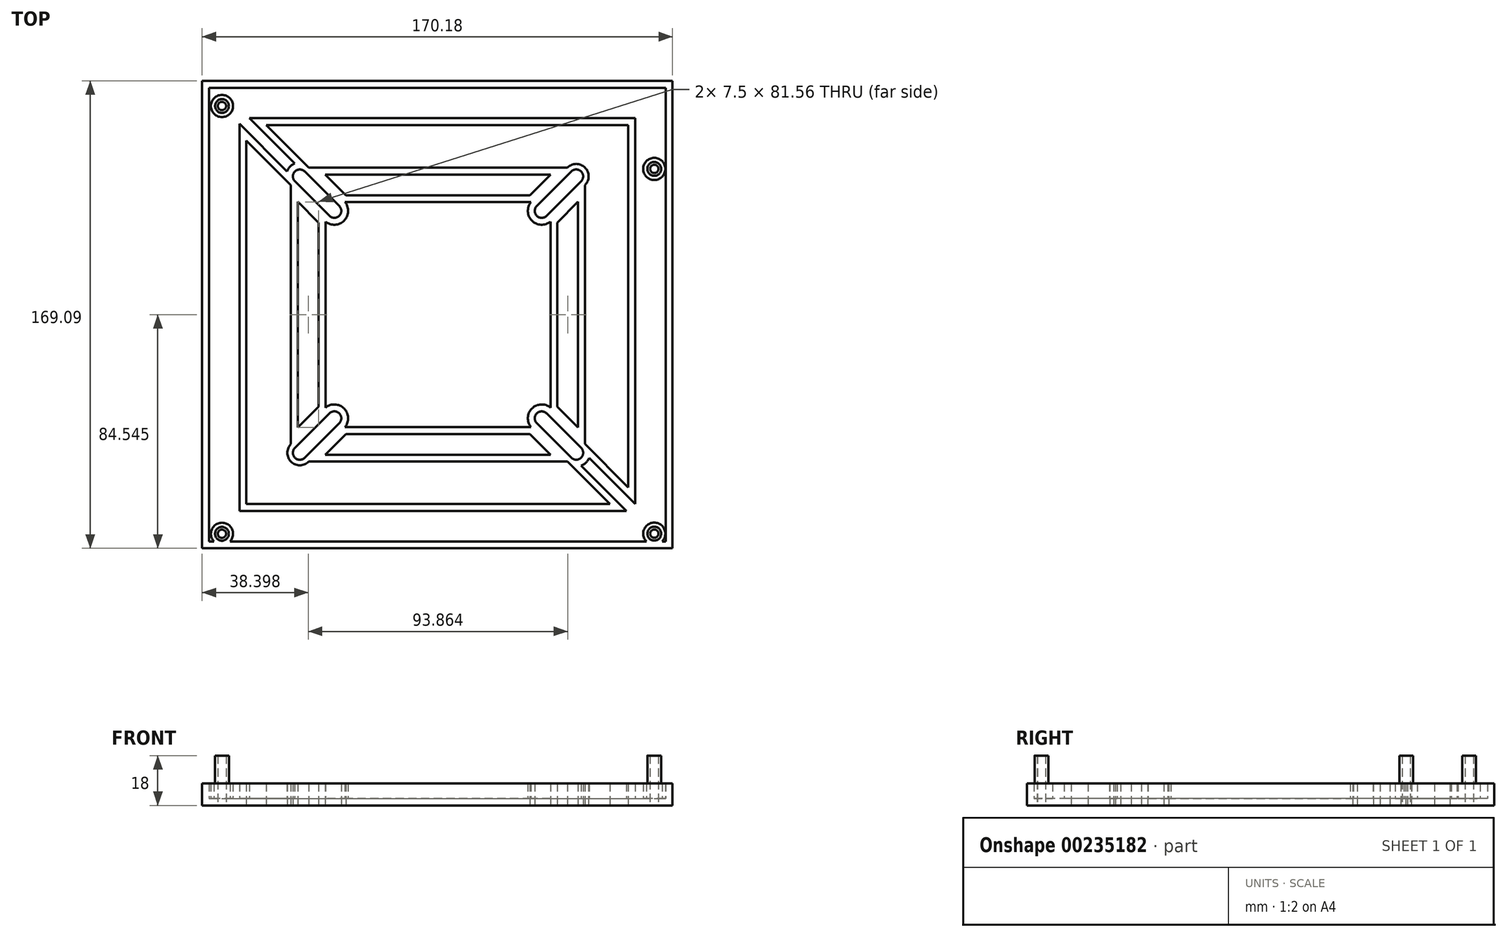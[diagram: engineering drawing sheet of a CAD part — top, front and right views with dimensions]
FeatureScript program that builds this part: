
annotation { "Feature Type Name" : "Feature", "Feature Type Description" : "" }
export const myFeature = defineFeature(function(context is Context, id is Id, definition is map)
    precondition{}
    {
        {
            var Q0;
            Q0=qCreatedBy(makeId("Top.planeOp"),FACE);
            var sketch = newSketch(context, id + "F0", { "sketchPlane" : qUnion([Q0])});
            skLineSegment(sketch, "E0.bottom", {"start": v(-27.19, 83.65) * mm, "end": v(142.99, 83.65) * mm});
            skLineSegment(sketch, "E0.top", {"start": v(-27.19, -85.44) * mm, "end": v(142.99, -85.44) * mm});
            skLineSegment(sketch, "E0.left", {"start": v(-27.19, 83.65) * mm, "end": v(-27.19, -85.44) * mm});
            skLineSegment(sketch, "E0.right", {"start": v(142.99, 83.65) * mm, "end": v(142.99, -85.44) * mm});
            skCircle(sketch, "E1", {"center": v(136.38, -80.15) * mm, "radius": 2.5 * mm});
            skCircle(sketch, "E2.0", {"center": v(136.38, -80.15) * mm, "radius": 1.5 * mm});
            skCircle(sketch, "E3", {"center": v(-20.03, -80.18) * mm, "radius": 2.5 * mm});
            skCircle(sketch, "E4.0", {"center": v(-20.03, -80.18) * mm, "radius": 1.5 * mm});
            skCircle(sketch, "E5", {"center": v(-20.02, 74.56) * mm, "radius": 2.5 * mm});
            skCircle(sketch, "E6.0", {"center": v(-20.02, 74.56) * mm, "radius": 1.5 * mm});
            skCircle(sketch, "E7", {"center": v(136.38, 51.8) * mm, "radius": 2.5 * mm});
            skCircle(sketch, "E8.0", {"center": v(136.38, 51.8) * mm, "radius": 1.5 * mm});
            skLineSegment(sketch, "E9.bottom", {"start": v(8.14, 49.1) * mm, "end": v(58.14, 49.1) * mm, "construction": true});
            skLineSegment(sketch, "E9.top", {"start": v(8.14, -50.9) * mm, "end": v(108.14, -50.9) * mm, "construction": true});
            skLineSegment(sketch, "E9.left", {"start": v(8.14, 49.1) * mm, "end": v(8.14, -0.9) * mm, "construction": true});
            skLineSegment(sketch, "E9.right", {"start": v(108.14, 49.1) * mm, "end": v(108.14, -0.9) * mm, "construction": true});
            skLineSegment(sketch, "E10.0", {"start": v(20.64, 36.6) * mm, "end": v(58.14, 36.6) * mm, "construction": true});
            skLineSegment(sketch, "E10.1", {"start": v(20.64, 36.6) * mm, "end": v(20.64, -0.9) * mm, "construction": true});
            skLineSegment(sketch, "E10.2", {"start": v(20.64, -38.4) * mm, "end": v(95.64, -38.4) * mm, "construction": true});
            skLineSegment(sketch, "E10.3", {"start": v(95.64, 36.6) * mm, "end": v(95.64, -0.9) * mm, "construction": true});
            skLineSegment(sketch, "E11", {"start": v(9.9, 50.87) * mm, "end": v(9.9, 50.87) * mm});
            skLineSegment(sketch, "E12", {"start": v(18.87, 34.84) * mm, "end": v(6.37, 47.34) * mm});
            skLineSegment(sketch, "E13", {"start": v(9.9, 50.87) * mm, "end": v(22.4, 38.37) * mm});
            skArc(sketch, "E14", {"start": v(6.37, 47.34) * mm, "mid": v(9.9, 47.34) * mm, "end": v(9.9, 50.87) * mm});
            skArc(sketch, "E15", {"start": v(9.9, 50.87) * mm, "mid": v(6.37, 50.87) * mm, "end": v(6.37, 47.34) * mm});
            skArc(sketch, "E16", {"start": v(22.4, 38.37) * mm, "mid": v(18.87, 38.37) * mm, "end": v(18.87, 34.84) * mm});
            skArc(sketch, "E17", {"start": v(18.87, 34.84) * mm, "mid": v(22.4, 34.84) * mm, "end": v(22.4, 38.37) * mm});
            skLineSegment(sketch, "E18.0", {"start": v(11.32, 52.29) * mm, "end": v(23.82, 39.79) * mm});
            skArc(sketch, "E18.1", {"start": v(11.32, 52.29) * mm, "mid": v(4.96, 52.29) * mm, "end": v(4.96, 45.92) * mm});
            skLineSegment(sketch, "E18.2", {"start": v(17.46, 33.42) * mm, "end": v(4.96, 45.92) * mm});
            skArc(sketch, "E18.3", {"start": v(17.46, 33.42) * mm, "mid": v(23.82, 33.42) * mm, "end": v(23.82, 39.79) * mm});
            skLineSegment(sketch, "E19", {"start": v(58.14, 36.6) * mm, "end": v(95.64, 36.6) * mm, "construction": true});
            skLineSegment(sketch, "E20", {"start": v(58.14, 49.1) * mm, "end": v(108.14, 49.1) * mm, "construction": true});
            skLineSegment(sketch, "E21", {"start": v(58.14, 36.6) * mm, "end": v(58.14, 49.1) * mm, "construction": true});
            skArc(sketch, "E22.MirrorCS", {"start": v(98.82, 33.42) * mm, "mid": v(92.46, 33.42) * mm, "end": v(92.46, 39.79) * mm});
            skArc(sketch, "E23.MirrorCS", {"start": v(97.4, 34.84) * mm, "mid": v(93.87, 34.84) * mm, "end": v(93.87, 38.37) * mm});
            skLineSegment(sketch, "E24.MirrorCS", {"start": v(98.82, 33.42) * mm, "end": v(111.32, 45.92) * mm});
            skLineSegment(sketch, "E25.MirrorCS", {"start": v(97.4, 34.84) * mm, "end": v(109.9, 47.34) * mm});
            skLineSegment(sketch, "E26.MirrorCS", {"start": v(106.37, 50.87) * mm, "end": v(93.87, 38.37) * mm});
            skLineSegment(sketch, "E27.MirrorCS", {"start": v(104.96, 52.29) * mm, "end": v(92.46, 39.79) * mm});
            skArc(sketch, "E28.MirrorCS", {"start": v(109.9, 47.34) * mm, "mid": v(106.37, 47.34) * mm, "end": v(106.37, 50.87) * mm});
            skArc(sketch, "E29.MirrorCS", {"start": v(106.37, 50.87) * mm, "mid": v(109.9, 50.87) * mm, "end": v(109.9, 47.34) * mm});
            skArc(sketch, "E30.MirrorCS", {"start": v(104.96, 52.29) * mm, "mid": v(111.32, 52.29) * mm, "end": v(111.32, 45.92) * mm});
            skArc(sketch, "E31.MirrorCS", {"start": v(93.87, 38.37) * mm, "mid": v(97.4, 38.37) * mm, "end": v(97.4, 34.84) * mm});
            skLineSegment(sketch, "E32", {"start": v(20.64, -0.9) * mm, "end": v(20.64, -38.4) * mm, "construction": true});
            skLineSegment(sketch, "E33", {"start": v(8.14, -0.9) * mm, "end": v(8.14, -50.9) * mm, "construction": true});
            skLineSegment(sketch, "E34", {"start": v(95.64, -0.9) * mm, "end": v(95.64, -38.4) * mm, "construction": true});
            skLineSegment(sketch, "E35", {"start": v(108.14, -0.9) * mm, "end": v(108.14, -50.9) * mm, "construction": true});
            skLineSegment(sketch, "E36", {"start": v(20.64, -0.9) * mm, "end": v(95.64, -0.9) * mm, "construction": true});
            skLineSegment(sketch, "E37.MirrorCS", {"start": v(17.46, -35.21) * mm, "end": v(4.96, -47.71) * mm});
            skLineSegment(sketch, "E38.MirrorCS", {"start": v(18.87, -36.63) * mm, "end": v(6.37, -49.13) * mm});
            skArc(sketch, "E39.MirrorCS", {"start": v(17.46, -35.21) * mm, "mid": v(23.82, -35.21) * mm, "end": v(23.82, -41.58) * mm});
            skArc(sketch, "E40.MirrorCS", {"start": v(18.87, -36.63) * mm, "mid": v(22.4, -36.63) * mm, "end": v(22.4, -40.16) * mm});
            skLineSegment(sketch, "E41.MirrorCS", {"start": v(9.9, -52.66) * mm, "end": v(22.4, -40.16) * mm});
            skLineSegment(sketch, "E42.MirrorCS", {"start": v(11.32, -54.08) * mm, "end": v(23.82, -41.58) * mm});
            skArc(sketch, "E43.MirrorCS", {"start": v(6.37, -49.13) * mm, "mid": v(9.9, -49.13) * mm, "end": v(9.9, -52.66) * mm});
            skArc(sketch, "E44.MirrorCS", {"start": v(9.9, -52.66) * mm, "mid": v(6.37, -52.66) * mm, "end": v(6.37, -49.13) * mm});
            skArc(sketch, "E45.MirrorCS", {"start": v(11.32, -54.08) * mm, "mid": v(4.96, -54.08) * mm, "end": v(4.96, -47.71) * mm});
            skArc(sketch, "E46.MirrorCS", {"start": v(22.4, -40.16) * mm, "mid": v(18.87, -40.16) * mm, "end": v(18.87, -36.63) * mm});
            skArc(sketch, "E47.MirrorCS", {"start": v(98.82, -35.21) * mm, "mid": v(92.46, -35.21) * mm, "end": v(92.46, -41.58) * mm});
            skArc(sketch, "E48.MirrorCS", {"start": v(97.4, -36.63) * mm, "mid": v(93.87, -36.63) * mm, "end": v(93.87, -40.16) * mm});
            skArc(sketch, "E49.MirrorCS", {"start": v(93.87, -40.16) * mm, "mid": v(97.4, -40.16) * mm, "end": v(97.4, -36.63) * mm});
            skLineSegment(sketch, "E50.MirrorCS", {"start": v(106.37, -52.66) * mm, "end": v(93.87, -40.16) * mm});
            skLineSegment(sketch, "E51.MirrorCS", {"start": v(97.4, -36.63) * mm, "end": v(109.9, -49.13) * mm});
            skLineSegment(sketch, "E52.MirrorCS", {"start": v(98.82, -35.21) * mm, "end": v(111.32, -47.71) * mm});
            skLineSegment(sketch, "E53.MirrorCS", {"start": v(104.96, -54.08) * mm, "end": v(92.46, -41.58) * mm});
            skArc(sketch, "E54.MirrorCS", {"start": v(109.9, -49.13) * mm, "mid": v(106.37, -49.13) * mm, "end": v(106.37, -52.66) * mm});
            skArc(sketch, "E55.MirrorCS", {"start": v(106.37, -52.66) * mm, "mid": v(109.9, -52.66) * mm, "end": v(109.9, -49.13) * mm});
            skArc(sketch, "E56.MirrorCS", {"start": v(104.96, -54.08) * mm, "mid": v(111.32, -54.08) * mm, "end": v(111.32, -47.71) * mm});
            skLineSegment(sketch, "E57", {"start": v(142.99, -85.44) * mm, "end": v(-27.19, 83.65) * mm, "construction": true});
            skLineSegment(sketch, "E58", {"start": v(142.99, 83.65) * mm, "end": v(-27.19, -85.44) * mm, "construction": true});
            skLineSegment(sketch, "E59.0", {"start": v(126.99, 67.65) * mm, "end": v(126.99, -69.44) * mm});
            skLineSegment(sketch, "E59.1", {"start": v(-11.19, 67.65) * mm, "end": v(126.99, 67.65) * mm});
            skLineSegment(sketch, "E59.2", {"start": v(-11.19, 67.65) * mm, "end": v(-11.19, -69.44) * mm});
            skLineSegment(sketch, "E59.3", {"start": v(-11.19, -69.44) * mm, "end": v(126.99, -69.44) * mm});
            skLineSegment(sketch, "E60", {"start": v(111.32, 45.92) * mm, "end": v(111.32, -47.71) * mm});
            skLineSegment(sketch, "E61", {"start": v(111.32, -47.71) * mm, "end": v(126.99, -63.38) * mm});
            skLineSegment(sketch, "E62", {"start": v(111.32, 45.92) * mm, "end": v(126.99, 61.59) * mm});
            skLineSegment(sketch, "E63", {"start": v(11.32, -54.08) * mm, "end": v(104.96, -54.08) * mm});
            skLineSegment(sketch, "E64", {"start": v(104.96, -54.08) * mm, "end": v(120.32, -69.44) * mm});
            skLineSegment(sketch, "E65", {"start": v(11.32, -54.08) * mm, "end": v(-4.04, -69.44) * mm});
            skLineSegment(sketch, "E66.MirrorCS", {"start": v(11.32, 52.29) * mm, "end": v(104.96, 52.29) * mm});
            skLineSegment(sketch, "E67.MirrorCS", {"start": v(104.96, 52.29) * mm, "end": v(120.32, 67.65) * mm});
            skLineSegment(sketch, "E68.MirrorCS", {"start": v(11.32, 52.29) * mm, "end": v(-4.04, 67.65) * mm});
            skLineSegment(sketch, "E69", {"start": v(4.96, -47.71) * mm, "end": v(-11.19, -63.86) * mm});
            skLineSegment(sketch, "E70", {"start": v(4.96, -47.71) * mm, "end": v(4.96, 45.92) * mm});
            skLineSegment(sketch, "E71", {"start": v(4.96, 45.92) * mm, "end": v(-11.19, 62.07) * mm});
            skLineSegment(sketch, "E72", {"start": v(98.82, 33.42) * mm, "end": v(98.82, -35.21) * mm});
            skLineSegment(sketch, "E73", {"start": v(92.46, -41.58) * mm, "end": v(23.82, -41.58) * mm});
            skLineSegment(sketch, "E74", {"start": v(17.46, -35.21) * mm, "end": v(17.46, 33.42) * mm});
            skLineSegment(sketch, "E75", {"start": v(23.82, 39.79) * mm, "end": v(92.46, 39.79) * mm});
            skLineSegment(sketch, "E76.0", {"start": v(91.42, -44.08) * mm, "end": v(24.86, -44.08) * mm});
            skLineSegment(sketch, "E76.1", {"start": v(98.92, -51.58) * mm, "end": v(91.42, -44.08) * mm});
            skLineSegment(sketch, "E76.2", {"start": v(17.36, -51.58) * mm, "end": v(98.92, -51.58) * mm});
            skLineSegment(sketch, "E76.3", {"start": v(17.36, -51.58) * mm, "end": v(24.86, -44.08) * mm});
            skLineSegment(sketch, "E77.0", {"start": v(101.32, 32.39) * mm, "end": v(101.32, -34.18) * mm});
            skLineSegment(sketch, "E77.1", {"start": v(101.32, 32.39) * mm, "end": v(108.82, 39.89) * mm});
            skLineSegment(sketch, "E77.2", {"start": v(108.82, 39.89) * mm, "end": v(108.82, -41.68) * mm});
            skLineSegment(sketch, "E77.3", {"start": v(101.32, -34.18) * mm, "end": v(108.82, -41.68) * mm});
            skLineSegment(sketch, "E78.0", {"start": v(24.86, 42.29) * mm, "end": v(91.42, 42.29) * mm});
            skLineSegment(sketch, "E78.1", {"start": v(17.36, 49.79) * mm, "end": v(24.86, 42.29) * mm});
            skLineSegment(sketch, "E78.2", {"start": v(17.36, 49.79) * mm, "end": v(98.92, 49.79) * mm});
            skLineSegment(sketch, "E78.3", {"start": v(98.92, 49.79) * mm, "end": v(91.42, 42.29) * mm});
            skLineSegment(sketch, "E79.0", {"start": v(14.96, -34.18) * mm, "end": v(14.96, 32.39) * mm});
            skLineSegment(sketch, "E79.1", {"start": v(14.96, -34.18) * mm, "end": v(7.46, -41.68) * mm});
            skLineSegment(sketch, "E79.2", {"start": v(7.46, -41.68) * mm, "end": v(7.46, 39.89) * mm});
            skLineSegment(sketch, "E79.3", {"start": v(14.96, 32.39) * mm, "end": v(7.46, 39.89) * mm});
            skSolve(sketch);
        }
        {
            var Q0;
            Q0=makeQuery(id+"F0.imprint","IMPRINT",FACE,{"disambiguationData":[TD([[makeQuery(id+"F0.imprint","IMPRINT",EDGE,{"derivedFrom":sQuery(id+"F0.wireOp",EDGE,"E0.bottom")}),-1.0]])]});
            var Q1;
            Q1=makeQuery(id+"F0.imprint","IMPRINT",FACE,{"disambiguationData":[TD([[makeQuery(id+"F0.imprint","IMPRINT",EDGE,{"derivedFrom":sQuery(id+"F0.wireOp",EDGE,"E12")}),1.0]])]});
            var Q2;
            Q2=makeQuery(id+"F0.imprint","IMPRINT",FACE,{"disambiguationData":[TD([[makeQuery(id+"F0.imprint","IMPRINT",EDGE,{"derivedFrom":sQuery(id+"F0.wireOp",EDGE,"E22.MirrorCS")}),-1.0]])]});
            var Q3;
            Q3=makeQuery(id+"F0.imprint","IMPRINT",FACE,{"disambiguationData":[TD([[makeQuery(id+"F0.imprint","IMPRINT",EDGE,{"derivedFrom":sQuery(id+"F0.wireOp",EDGE,"E47.MirrorCS")}),1.0]])]});
            var Q4;
            Q4=makeQuery(id+"F0.imprint","IMPRINT",FACE,{"disambiguationData":[TD([[makeQuery(id+"F0.imprint","IMPRINT",EDGE,{"derivedFrom":sQuery(id+"F0.wireOp",EDGE,"E37.MirrorCS")}),1.0]])]});
            var Q5;
            Q5=makeQuery(id+"F0.imprint","IMPRINT",FACE,{"disambiguationData":[TD([[makeQuery(id+"F0.imprint","IMPRINT",EDGE,{"derivedFrom":sQuery(id+"F0.wireOp",EDGE,"E5")}),1.0]])]});
            var Q6;
            Q6=makeQuery(id+"F0.imprint","IMPRINT",FACE,{"disambiguationData":[TD([[makeQuery(id+"F0.imprint","IMPRINT",EDGE,{"derivedFrom":sQuery(id+"F0.wireOp",EDGE,"E7")}),1.0]])]});
            var Q7;
            Q7=makeQuery(id+"F0.imprint","IMPRINT",FACE,{"disambiguationData":[TD([[makeQuery(id+"F0.imprint","IMPRINT",EDGE,{"derivedFrom":sQuery(id+"F0.wireOp",EDGE,"E1")}),1.0]])]});
            var Q8;
            Q8=makeQuery(id+"F0.imprint","IMPRINT",FACE,{"disambiguationData":[TD([[makeQuery(id+"F0.imprint","IMPRINT",EDGE,{"derivedFrom":sQuery(id+"F0.wireOp",EDGE,"E3")}),1.0]])]});
            var Q9;
            Q9=makeQuery(id+"F0.imprint","IMPRINT",FACE,{"disambiguationData":[TD([[makeQuery(id+"F0.imprint","IMPRINT",EDGE,{"derivedFrom":sQuery(id+"F0.wireOp",EDGE,"E56.MirrorCS")}),-1.0]])]});
            var Q10;
            Q10=makeQuery(id+"F0.imprint","IMPRINT",FACE,{"disambiguationData":[TD([[makeQuery(id+"F0.imprint","IMPRINT",EDGE,{"derivedFrom":sQuery(id+"F0.wireOp",EDGE,"E45.MirrorCS")}),1.0]])]});
            var Q11;
            Q11=makeQuery(id+"F0.imprint","IMPRINT",FACE,{"disambiguationData":[TD([[makeQuery(id+"F0.imprint","IMPRINT",EDGE,{"derivedFrom":sQuery(id+"F0.wireOp",EDGE,"E42.MirrorCS")}),-1.0]])]});
            var Q12;
            Q12=makeQuery(id+"F0.imprint","IMPRINT",FACE,{"disambiguationData":[TD([[makeQuery(id+"F0.imprint","IMPRINT",EDGE,{"derivedFrom":sQuery(id+"F0.wireOp",EDGE,"E24.MirrorCS")}),-1.0]])]});
            var Q13;
            Q13=makeQuery(id+"F0.imprint","IMPRINT",FACE,{"disambiguationData":[TD([[makeQuery(id+"F0.imprint","IMPRINT",EDGE,{"derivedFrom":sQuery(id+"F0.wireOp",EDGE,"E18.2")}),1.0]])]});
            var Q14;
            Q14=makeQuery(id+"F0.imprint","IMPRINT",FACE,{"disambiguationData":[TD([[makeQuery(id+"F0.imprint","IMPRINT",EDGE,{"derivedFrom":sQuery(id+"F0.wireOp",EDGE,"E18.0")}),1.0]])]});
            var Q15;
            Q15=makeQuery(id+"F0.imprint","IMPRINT",FACE,{"disambiguationData":[TD([[makeQuery(id+"F0.imprint","IMPRINT",EDGE,{"derivedFrom":sQuery(id+"F0.wireOp",EDGE,"E30.MirrorCS")}),1.0]])]});
            var Q16;
            Q16=makeQuery(id+"F0.imprint","IMPRINT",FACE,{"disambiguationData":[TD([[makeQuery(id+"F0.imprint","IMPRINT",EDGE,{"derivedFrom":sQuery(id+"F0.wireOp",EDGE,"E18.1")}),-1.0]])]});
            extrude(context, id + "F1", {"entities" : qUnion([Q0, Q1, Q2, Q3, Q4, Q5, Q6, Q7, Q8, Q9, Q10, Q11, Q12, Q13, Q14, Q15, Q16]), "depth" : 8 * mm});
        }
        {
            var Q0;
            Q0=makeQuery(id+"F1.opExtrude","CAP_FACE",FACE,{"disambiguationData":[OSD([sQuery(id+"F0.wireOp",EDGE,"E0.bottom"),sQuery(id+"F0.wireOp",EDGE,"E0.top"),sQuery(id+"F0.wireOp",EDGE,"E0.left"),sQuery(id+"F0.wireOp",EDGE,"E0.right"),sQuery(id+"F0.wireOp",EDGE,"E2.0"),sQuery(id+"F0.wireOp",EDGE,"E4.0"),sQuery(id+"F0.wireOp",EDGE,"E6.0"),sQuery(id+"F0.wireOp",EDGE,"E8.0"),sQuery(id+"F0.wireOp",EDGE,"E12"),sQuery(id+"F0.wireOp",EDGE,"E13"),sQuery(id+"F0.wireOp",EDGE,"E15"),sQuery(id+"F0.wireOp",EDGE,"E17"),sQuery(id+"F0.wireOp",EDGE,"E18.3"),sQuery(id+"F0.wireOp",EDGE,"E22.MirrorCS"),sQuery(id+"F0.wireOp",EDGE,"E23.MirrorCS"),sQuery(id+"F0.wireOp",EDGE,"E25.MirrorCS"),sQuery(id+"F0.wireOp",EDGE,"E26.MirrorCS"),sQuery(id+"F0.wireOp",EDGE,"E29.MirrorCS"),sQuery(id+"F0.wireOp",EDGE,"E38.MirrorCS"),sQuery(id+"F0.wireOp",EDGE,"E39.MirrorCS"),sQuery(id+"F0.wireOp",EDGE,"E40.MirrorCS"),sQuery(id+"F0.wireOp",EDGE,"E41.MirrorCS"),sQuery(id+"F0.wireOp",EDGE,"E44.MirrorCS"),sQuery(id+"F0.wireOp",EDGE,"E47.MirrorCS"),sQuery(id+"F0.wireOp",EDGE,"E48.MirrorCS"),sQuery(id+"F0.wireOp",EDGE,"E50.MirrorCS"),sQuery(id+"F0.wireOp",EDGE,"E51.MirrorCS"),sQuery(id+"F0.wireOp",EDGE,"E55.MirrorCS"),sQuery(id+"F0.wireOp",EDGE,"E59.0"),sQuery(id+"F0.wireOp",EDGE,"E59.1"),sQuery(id+"F0.wireOp",EDGE,"E59.2"),sQuery(id+"F0.wireOp",EDGE,"E59.3"),sQuery(id+"F0.wireOp",EDGE,"E60"),sQuery(id+"F0.wireOp",EDGE,"E61"),sQuery(id+"F0.wireOp",EDGE,"E62"),sQuery(id+"F0.wireOp",EDGE,"E63"),sQuery(id+"F0.wireOp",EDGE,"E64"),sQuery(id+"F0.wireOp",EDGE,"E65"),sQuery(id+"F0.wireOp",EDGE,"E66.MirrorCS"),sQuery(id+"F0.wireOp",EDGE,"E67.MirrorCS"),sQuery(id+"F0.wireOp",EDGE,"E68.MirrorCS"),sQuery(id+"F0.wireOp",EDGE,"E69"),sQuery(id+"F0.wireOp",EDGE,"E70"),sQuery(id+"F0.wireOp",EDGE,"E71"),sQuery(id+"F0.wireOp",EDGE,"E72"),sQuery(id+"F0.wireOp",EDGE,"E73"),sQuery(id+"F0.wireOp",EDGE,"E74"),sQuery(id+"F0.wireOp",EDGE,"E75")])],"isStart":false});
            shell(context, id + "F2", {"entities" : qUnion([Q0]), "thickness" : 2.5 * mm});
        }
        {
            var Q0;
            {var subQ0=sQuery(id+"F0.wireOp",EDGE,"E79.3");var subQ1=sQuery(id+"F0.wireOp",EDGE,"E79.2");var subQ2=sQuery(id+"F0.wireOp",EDGE,"E79.1");var subQ3=sQuery(id+"F0.wireOp",EDGE,"E79.0");var subQ4=sQuery(id+"F0.wireOp",EDGE,"E78.3");var subQ5=sQuery(id+"F0.wireOp",EDGE,"E78.2");var subQ6=sQuery(id+"F0.wireOp",EDGE,"E78.1");var subQ7=sQuery(id+"F0.wireOp",EDGE,"E78.0");var subQ8=sQuery(id+"F0.wireOp",EDGE,"E77.3");var subQ9=sQuery(id+"F0.wireOp",EDGE,"E77.2");var subQ10=sQuery(id+"F0.wireOp",EDGE,"E77.1");var subQ11=sQuery(id+"F0.wireOp",EDGE,"E77.0");var subQ12=sQuery(id+"F0.wireOp",EDGE,"E76.3");var subQ13=sQuery(id+"F0.wireOp",EDGE,"E76.2");var subQ14=sQuery(id+"F0.wireOp",EDGE,"E76.1");var subQ15=sQuery(id+"F0.wireOp",EDGE,"E76.0");var subQ16=sQuery(id+"F0.wireOp",EDGE,"E75");var subQ17=sQuery(id+"F0.wireOp",EDGE,"E74");var subQ18=sQuery(id+"F0.wireOp",EDGE,"E73");var subQ19=sQuery(id+"F0.wireOp",EDGE,"E72");var subQ20=sQuery(id+"F0.wireOp",EDGE,"E71");var subQ21=sQuery(id+"F0.wireOp",EDGE,"E70");var subQ22=sQuery(id+"F0.wireOp",EDGE,"E69");var subQ23=sQuery(id+"F0.wireOp",EDGE,"E68.MirrorCS");var subQ24=sQuery(id+"F0.wireOp",EDGE,"E67.MirrorCS");var subQ25=sQuery(id+"F0.wireOp",EDGE,"E66.MirrorCS");var subQ26=sQuery(id+"F0.wireOp",EDGE,"E65");var subQ27=sQuery(id+"F0.wireOp",EDGE,"E64");var subQ28=sQuery(id+"F0.wireOp",EDGE,"E63");var subQ29=sQuery(id+"F0.wireOp",EDGE,"E62");var subQ30=sQuery(id+"F0.wireOp",EDGE,"E61");var subQ31=sQuery(id+"F0.wireOp",EDGE,"E60");var subQ32=sQuery(id+"F0.wireOp",EDGE,"E59.3");var subQ33=sQuery(id+"F0.wireOp",EDGE,"E59.2");var subQ34=sQuery(id+"F0.wireOp",EDGE,"E59.1");var subQ35=sQuery(id+"F0.wireOp",EDGE,"E59.0");var subQ36=sQuery(id+"F0.wireOp",EDGE,"E55.MirrorCS");var subQ37=sQuery(id+"F0.wireOp",EDGE,"E51.MirrorCS");var subQ38=sQuery(id+"F0.wireOp",EDGE,"E50.MirrorCS");var subQ39=sQuery(id+"F0.wireOp",EDGE,"E48.MirrorCS");var subQ40=sQuery(id+"F0.wireOp",EDGE,"E47.MirrorCS");var subQ41=sQuery(id+"F0.wireOp",EDGE,"E44.MirrorCS");var subQ42=sQuery(id+"F0.wireOp",EDGE,"E41.MirrorCS");var subQ43=sQuery(id+"F0.wireOp",EDGE,"E40.MirrorCS");var subQ44=sQuery(id+"F0.wireOp",EDGE,"E39.MirrorCS");var subQ45=sQuery(id+"F0.wireOp",EDGE,"E38.MirrorCS");var subQ46=sQuery(id+"F0.wireOp",EDGE,"E29.MirrorCS");var subQ47=sQuery(id+"F0.wireOp",EDGE,"E26.MirrorCS");var subQ48=sQuery(id+"F0.wireOp",EDGE,"E25.MirrorCS");var subQ49=sQuery(id+"F0.wireOp",EDGE,"E23.MirrorCS");var subQ50=sQuery(id+"F0.wireOp",EDGE,"E22.MirrorCS");var subQ51=sQuery(id+"F0.wireOp",EDGE,"E18.3");var subQ52=sQuery(id+"F0.wireOp",EDGE,"E17");var subQ53=sQuery(id+"F0.wireOp",EDGE,"E15");var subQ54=sQuery(id+"F0.wireOp",EDGE,"E13");var subQ55=sQuery(id+"F0.wireOp",EDGE,"E12");var subQ56=sQuery(id+"F0.wireOp",EDGE,"E8.0");var subQ57=sQuery(id+"F0.wireOp",EDGE,"E6.0");var subQ58=sQuery(id+"F0.wireOp",EDGE,"E4.0");var subQ59=sQuery(id+"F0.wireOp",EDGE,"E2.0");var subQ60=sQuery(id+"F0.wireOp",EDGE,"E0.right");var subQ61=sQuery(id+"F0.wireOp",EDGE,"E0.left");var subQ62=sQuery(id+"F0.wireOp",EDGE,"E0.top");var subQ63=sQuery(id+"F0.wireOp",EDGE,"E0.bottom");Q0=makeQuery(id+"F2.opShell","OFFSET_FACE",FACE,{"disambiguationData":[OSD([subQ63,subQ62,subQ61,subQ60,subQ59,subQ58,subQ57,subQ56,subQ55,subQ54,subQ53,subQ52,subQ51,subQ50,subQ49,subQ48,subQ47,subQ46,subQ45,subQ44,subQ43,subQ42,subQ41,subQ40,subQ39,subQ38,subQ37,subQ36,subQ35,subQ34,subQ33,subQ32,subQ31,subQ30,subQ29,subQ28,subQ27,subQ26,subQ25,subQ24,subQ23,subQ22,subQ21,subQ20,subQ19,subQ18,subQ17,subQ16,subQ15,subQ14,subQ13,subQ12,subQ11,subQ10,subQ9,subQ8,subQ7,subQ6,subQ5,subQ4,subQ3,subQ2,subQ1,subQ0]),TDD([makeQuery(id+"F1.opExtrude","CAP_FACE",FACE,{"disambiguationData":[OSD([subQ63,subQ62,subQ61,subQ60,subQ59,subQ58,subQ57,subQ56,subQ55,subQ54,subQ53,subQ52,subQ51,subQ50,subQ49,subQ48,subQ47,subQ46,subQ45,subQ44,subQ43,subQ42,subQ41,subQ40,subQ39,subQ38,subQ37,subQ36,subQ35,subQ34,subQ33,subQ32,subQ31,subQ30,subQ29,subQ28,subQ27,subQ26,subQ25,subQ24,subQ23,subQ22,subQ21,subQ20,subQ19,subQ18,subQ17,subQ16,subQ15,subQ14,subQ13,subQ12,subQ11,subQ10,subQ9,subQ8,subQ7,subQ6,subQ5,subQ4,subQ3,subQ2,subQ1,subQ0])],"isStart":false})]),OD(2.0)]});}
            var sketch = newSketch(context, id + "F3", { "sketchPlane" : qUnion([Q0])});
            skCircle(sketch, "E80.0", {"center": v(136.38, -80.15) * mm, "radius": 1.5 * mm});
            skCircle(sketch, "E80.1", {"center": v(136.38, 51.8) * mm, "radius": 1.5 * mm});
            skCircle(sketch, "E80.2", {"center": v(-20.02, 74.56) * mm, "radius": 1.5 * mm});
            skCircle(sketch, "E80.3", {"center": v(-20.03, -80.18) * mm, "radius": 1.5 * mm});
            skCircle(sketch, "E81.0", {"center": v(136.38, 51.8) * mm, "radius": 2.5 * mm});
            skCircle(sketch, "E82.0", {"center": v(-20.03, -80.18) * mm, "radius": 2.5 * mm});
            skCircle(sketch, "E83.0", {"center": v(136.38, -80.15) * mm, "radius": 2.5 * mm});
            skCircle(sketch, "E84.0", {"center": v(-20.02, 74.56) * mm, "radius": 2.5 * mm});
            skSolve(sketch);
        }
        {
            var Q0;
            Q0=makeQuery(id+"F3.imprint","IMPRINT",FACE,{"disambiguationData":[TD([[makeQuery(id+"F3.imprint","IMPRINT",EDGE,{"derivedFrom":sQuery(id+"F3.wireOp",EDGE,"E80.1")}),-1.0]])]});
            var Q1;
            Q1=makeQuery(id+"F3.imprint","IMPRINT",FACE,{"disambiguationData":[TD([[makeQuery(id+"F3.imprint","IMPRINT",EDGE,{"derivedFrom":sQuery(id+"F3.wireOp",EDGE,"E80.2")}),-1.0]])]});
            var Q2;
            Q2=makeQuery(id+"F3.imprint","IMPRINT",FACE,{"disambiguationData":[TD([[makeQuery(id+"F3.imprint","IMPRINT",EDGE,{"derivedFrom":sQuery(id+"F3.wireOp",EDGE,"E80.3")}),-1.0]])]});
            var Q3;
            Q3=makeQuery(id+"F3.imprint","IMPRINT",FACE,{"disambiguationData":[TD([[makeQuery(id+"F3.imprint","IMPRINT",EDGE,{"derivedFrom":sQuery(id+"F3.wireOp",EDGE,"E80.0")}),-1.0]])]});
            extrude(context, id + "F4", {"entities" : qUnion([Q0, Q1, Q2, Q3]), "operationType" : NewBodyOperationType.ADD, "depth" : 10 * mm});
        }
    });
